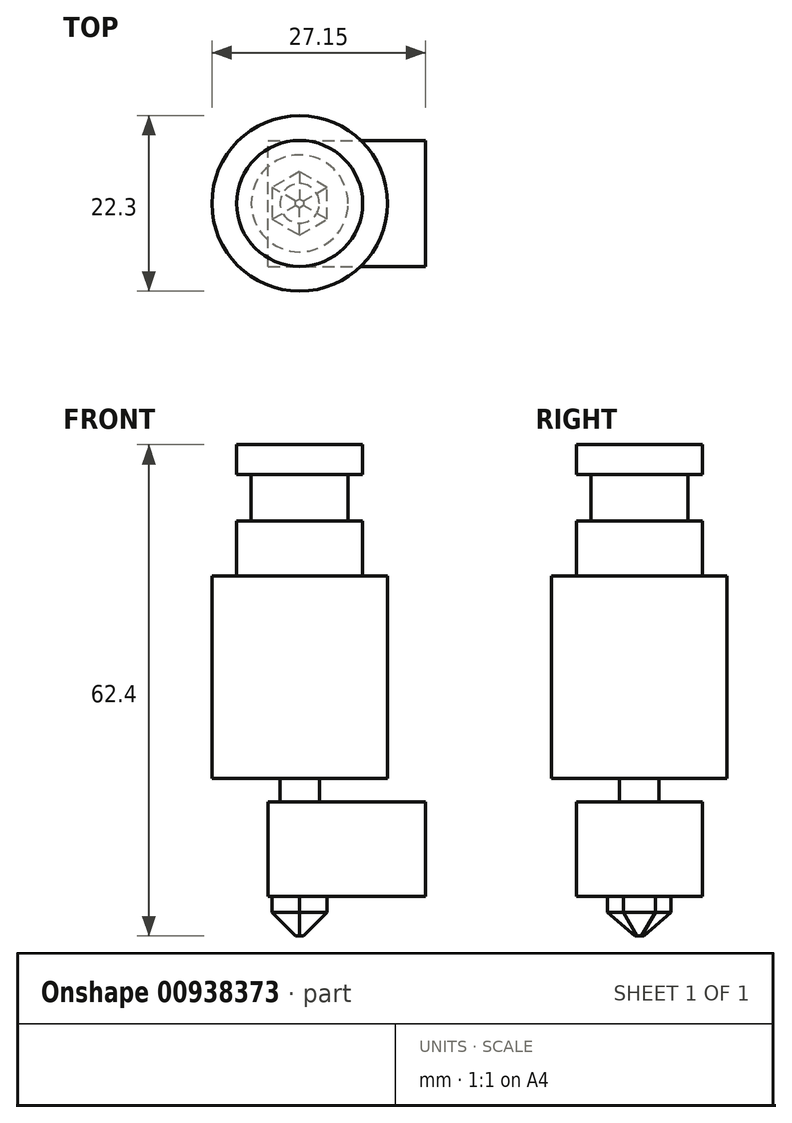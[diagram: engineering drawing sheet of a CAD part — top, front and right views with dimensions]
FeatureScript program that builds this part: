
annotation { "Feature Type Name" : "Feature", "Feature Type Description" : "" }
export const myFeature = defineFeature(function(context is Context, id is Id, definition is map)
    precondition{}
    {
        {
            var Q0;
            Q0=qCreatedBy(makeId("Top.planeOp"),FACE);
            var sketch = newSketch(context, id + "F0", { "sketchPlane" : qUnion([Q0])});
            skCircle(sketch, "E0", {"center": v(0, 0) * mm, "radius": 8 * mm});
            skSolve(sketch);
        }
        {
            var Q0;
            Q0 = qSketchRegion(id + "F0", true);
            extrude(context, id + "F1", {"entities" : qUnion([Q0]), "oppositeDirection" : true, "depth" : 3.8 * mm, "offsetDistance" : 25 * mm});
        }
        {
            var Q0;
            Q0=makeQuery(id+"F1.opExtrude","CAP_FACE",FACE,{"disambiguationData":[OSD([sQuery(id+"F0.wireOp",EDGE,"E0")])],"isStart":false});
            var sketch = newSketch(context, id + "F2", { "sketchPlane" : qUnion([Q0])});
            skCircle(sketch, "E1", {"center": v(0, 0) * mm, "radius": 6.15 * mm});
            skSolve(sketch);
        }
        {
            var Q0;
            Q0=makeQuery(id+"F2.imprint","IMPRINT",FACE,{"disambiguationData":[TD([[makeQuery(id+"F2.imprint","IMPRINT",EDGE,{"derivedFrom":sQuery(id+"F2.wireOp",EDGE,"E1")}),1.0]])]});
            extrude(context, id + "F3", {"entities" : qUnion([Q0]), "operationType" : NewBodyOperationType.ADD, "depth" : 5.9 * mm, "offsetDistance" : 25 * mm});
        }
        {
            var Q0;
            Q0=makeQuery(id+"F3.opExtrude","CAP_FACE",FACE,{"disambiguationData":[OSD([sQuery(id+"F2.wireOp",EDGE,"E1")])],"isStart":false});
            var sketch = newSketch(context, id + "F4", { "sketchPlane" : qUnion([Q0])});
            skCircle(sketch, "E2", {"center": v(0, 0) * mm, "radius": 8 * mm});
            skSolve(sketch);
        }
        {
            var Q0;
            Q0 = qSketchRegion(id + "F4", true);
            extrude(context, id + "F5", {"entities" : qUnion([Q0]), "operationType" : NewBodyOperationType.ADD, "depth" : 7 * mm, "offsetDistance" : 25 * mm});
        }
        {
            var Q0;
            Q0=makeQuery(id+"F5.opExtrude","CAP_FACE",FACE,{"disambiguationData":[OSD([sQuery(id+"F4.wireOp",EDGE,"E2")])],"isStart":false});
            var sketch = newSketch(context, id + "F6", { "sketchPlane" : qUnion([Q0])});
            skCircle(sketch, "E3", {"center": v(0, 0) * mm, "radius": 11.15 * mm});
            skSolve(sketch);
        }
        {
            var Q0;
            Q0 = qSketchRegion(id + "F6", true);
            extrude(context, id + "F7", {"entities" : qUnion([Q0]), "operationType" : NewBodyOperationType.ADD, "depth" : 25.7 * mm, "offsetDistance" : 25 * mm});
        }
        {
            var Q0;
            Q0=makeQuery(id+"F7.opExtrude","CAP_FACE",FACE,{"disambiguationData":[OSD([sQuery(id+"F6.wireOp",EDGE,"E3")])],"isStart":false});
            var sketch = newSketch(context, id + "F8", { "sketchPlane" : qUnion([Q0])});
            skCircle(sketch, "E4", {"center": v(0, 0) * mm, "radius": 2.5 * mm});
            skSolve(sketch);
        }
        {
            var Q0;
            Q0 = qSketchRegion(id + "F8", true);
            extrude(context, id + "F9", {"entities" : qUnion([Q0]), "operationType" : NewBodyOperationType.ADD, "depth" : 3 * mm, "offsetDistance" : 25 * mm});
        }
        {
            var Q0;
            Q0=makeQuery(id+"F9.opExtrude","CAP_FACE",FACE,{"disambiguationData":[OSD([sQuery(id+"F8.wireOp",EDGE,"E4")])],"isStart":false});
            var sketch = newSketch(context, id + "F10", { "sketchPlane" : qUnion([Q0])});
            skLineSegment(sketch, "E5.bottom", {"start": v(-4, 8) * mm, "end": v(16, 8) * mm});
            skLineSegment(sketch, "E5.top", {"start": v(-4, -8) * mm, "end": v(16, -8) * mm});
            skLineSegment(sketch, "E5.left", {"start": v(-4, 8) * mm, "end": v(-4, -8) * mm});
            skLineSegment(sketch, "E5.right", {"start": v(16, 8) * mm, "end": v(16, -8) * mm});
            skPoint(sketch, "E6", {"position": v(16, 0) * mm});
            skLineSegment(sketch, "E7", {"start": v(38.28, 0) * mm, "end": v(-24.46, 0) * mm, "construction": true});
            skPoint(sketch, "E8", {"position": v(0, 0) * mm});
            skSolve(sketch);
        }
        {
            var Q0;
            Q0=makeQuery(id+"F10.imprint","IMPRINT",FACE,{"disambiguationData":[TD([[makeQuery(id+"F10.imprint","IMPRINT",EDGE,{"derivedFrom":sQuery(id+"F10.wireOp",EDGE,"E5.bottom")}),-1.0]])]});
            var Q1;
            Q1=makeQuery(id+"F10.imprint","IMPRINT",FACE,{"disambiguationData":[TD([[makeQuery(id+"F10.imprint","IMPRINT",EDGE,{"derivedFrom":makeQuery(id+"F9.opExtrude","CAP_EDGE",EDGE,{"disambiguationData":[OSD([sQuery(id+"F8.wireOp",EDGE,"E4")])],"isStart":false})}),1.0]])]});
            extrude(context, id + "F11", {"entities" : qUnion([Q0, Q1]), "operationType" : NewBodyOperationType.ADD, "depth" : 12 * mm, "offsetDistance" : 25 * mm});
        }
        {
            var Q0;
            Q0=makeQuery(id+"F11.opExtrude","CAP_FACE",FACE,{"disambiguationData":[OSD([sQuery(id+"F10.wireOp",EDGE,"E5.bottom"),sQuery(id+"F10.wireOp",EDGE,"E5.top"),sQuery(id+"F10.wireOp",EDGE,"E5.left"),sQuery(id+"F10.wireOp",EDGE,"E5.right")])],"isStart":false});
            var sketch = newSketch(context, id + "F12", { "sketchPlane" : qUnion([Q0])});
            skCircle(sketch, "E9.cCircle", {"center": v(0, 0) * mm, "radius": 3.5 * mm, "construction": true});
            skLineSegment(sketch, "E9.0", {"start": v(3.5, -2.02) * mm, "end": v(0, -4.04) * mm});
            skLineSegment(sketch, "E9.1", {"start": v(0, -4.04) * mm, "end": v(-3.5, -2.02) * mm});
            skLineSegment(sketch, "E9.2", {"start": v(-3.5, -2.02) * mm, "end": v(-3.5, 2.02) * mm});
            skLineSegment(sketch, "E9.3", {"start": v(-3.5, 2.02) * mm, "end": v(0, 4.04) * mm});
            skLineSegment(sketch, "E9.4", {"start": v(0, 4.04) * mm, "end": v(3.5, 2.02) * mm});
            skLineSegment(sketch, "E9.5", {"start": v(3.5, 2.02) * mm, "end": v(3.5, -2.02) * mm});
            skPoint(sketch, "E9.0.midPoint", {"position": v(1.75, -3.03) * mm});
            skPoint(sketch, "E10", {"position": v(16, 0) * mm});
            skLineSegment(sketch, "E11", {"start": v(23.8, 0) * mm, "end": v(-18.09, 0) * mm, "construction": true});
            skSolve(sketch);
        }
        {
            var Q0;
            Q0=makeQuery(id+"F12.imprint","IMPRINT",FACE,{"disambiguationData":[TD([[makeQuery(id+"F12.imprint","IMPRINT",EDGE,{"derivedFrom":sQuery(id+"F12.wireOp",EDGE,"E9.0")}),-1.0]])]});
            extrude(context, id + "F13", {"entities" : qUnion([Q0]), "operationType" : NewBodyOperationType.ADD, "depth" : 5 * mm, "offsetDistance" : 25 * mm});
        }
        {
            var Q0;
            Q0=makeQuery(id+"F13.opExtrude","CAP_EDGE",EDGE,{"disambiguationData":[OSD([sQuery(id+"F12.wireOp",EDGE,"E9.5")])],"isStart":false});
            var Q1;
            Q1=makeQuery(id+"F13.opExtrude","CAP_EDGE",EDGE,{"disambiguationData":[OSD([sQuery(id+"F12.wireOp",EDGE,"E9.4")])],"isStart":false});
            var Q2;
            Q2=makeQuery(id+"F13.opExtrude","CAP_EDGE",EDGE,{"disambiguationData":[OSD([sQuery(id+"F12.wireOp",EDGE,"E9.3")])],"isStart":false});
            var Q3;
            Q3=makeQuery(id+"F13.opExtrude","CAP_EDGE",EDGE,{"disambiguationData":[OSD([sQuery(id+"F12.wireOp",EDGE,"E9.2")])],"isStart":false});
            var Q4;
            Q4=makeQuery(id+"F13.opExtrude","CAP_EDGE",EDGE,{"disambiguationData":[OSD([sQuery(id+"F12.wireOp",EDGE,"E9.0")])],"isStart":false});
            var Q5;
            Q5=makeQuery(id+"F13.opExtrude","CAP_EDGE",EDGE,{"disambiguationData":[OSD([sQuery(id+"F12.wireOp",EDGE,"E9.1")])],"isStart":false});
            chamfer(context, id + "F14", {"entities" : qUnion([Q0, Q1, Q2, Q3, Q4, Q5]), "width" : 3 * mm, "tangentPropagation" : true});
        }
    });
